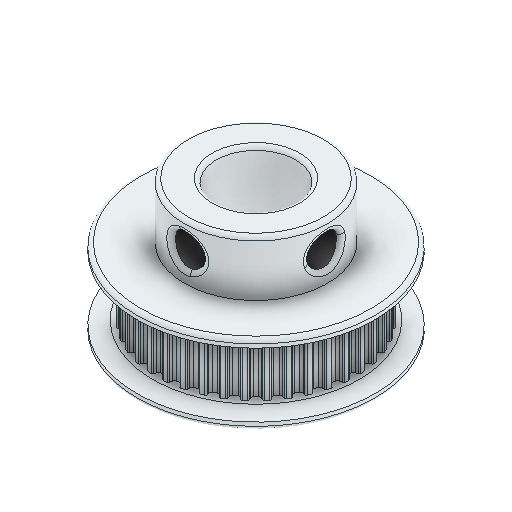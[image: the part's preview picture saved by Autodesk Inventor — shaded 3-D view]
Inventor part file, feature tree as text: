
AUTODESK INVENTOR PART (.ipt)
format: ipt  version: 2025.1 (Build 291241000, 241)  size: 604,160 bytes
history: native  units: mm
features: other x1, chamfer x1
ambient origin geometry x8: Origin, YZ Plane, XZ Plane, XY Plane, X Axis, Y Axis, Z Axis, Center Point
bodies: Body1 (feature_tree)
feature tree (2):
  other  "Bryła1"
  chamfer  "Chamfer2"  [1 undecoded]
note: 1 required parameter value undecoded (feature->parameter linkage not recoverable at this tier; creation-order binding heuristic only, values carry confidence <= 0.55)
